# Revit family: Cabinet-Specimen_Pass_Thru-Whitehall-WH1865_Series
name_source: partatom
category: Specialty Equipment
units: mm (PartAtom-declared; Revit-internal decimal feet)

## family parameters
Cut with Voids When Loaded = No
Host = Face
OmniClass Number = 23.65.70.17.27
OmniClass Title = Fire Extinguishers
Part Type = Normal
Room Calculation Point = No
Round Connector Dimension = Use Diameter
Shared = Yes

## types (2) — shared parameters
Assembly Code = D4030200
Default Elevation = 36"
Description = Specimen Pass-Thru Cabinet
Door Height = 12 1/2"
Door Length = 12 1/2"
Height = 14 1/2"
Installation Type = Recessed Wall Mounted
Length = 14 1/2"
Manufacturer = Whitehall Manufacturing
Product Documentation Link = https://www.whitehallmfg.com
Product Page URL = https://www.whitehallmfg.com
URL = http://www.whitehallmfg.com
Wall Thickness (Must Specify) = 3"
Wall Thickness Constraints = 3"
Width = 6 1/4"

## per-type parameters (varying)
| type | Body Material | Material |
| WH1865 | Stainless Steel-Whitehall-Satin | Stainless Steel-Whitehall-Satin |
| WH1865-EG10 | Stainless Steel-Whitehall-Enviro-glaze Powder Coat Snow White | Stainless Steel-Whitehall-Enviro-glaze Powder Coat Snow White |

note: column(s) folded — value = type name in every type: Model

## geometry (parser evidence)
native form markers: Sweep x3
no freeform markers — native parametric forms only
